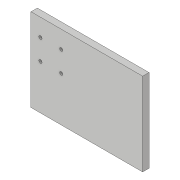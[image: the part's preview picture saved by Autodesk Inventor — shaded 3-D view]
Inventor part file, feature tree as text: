
AUTODESK INVENTOR PART (.ipt)
format: ipt  version: 2019 (Build 230136000, 136)  size: 96,768 bytes
history: native  units: mm
features: sketch x4, extrude x2
ambient origin geometry x8: Origin, YZ Plane, XZ Plane, XY Plane, X Axis, Y Axis, Z Axis, Center Point
bodies: Solid1 (feature_tree)
feature tree (6):
  extrude  "Extrusion1"  Depth=260.0mm
  sketch  "Sketch2"  dims[d2=20.0mm d3=0.0mm d4=30.0mm]
  sketch  "Sketch3"  dims[d5=55.0mm]
  extrude  "Extrusion2"  Depth=20.0mm
  sketch  "Sketch1"  dims[d0=350.0mm d1=260.0mm]
  sketch  "Sketch4"  dims[d6=55.0mm d7=65.0mm d8=65.0mm d9=10.0mm d10=10.0mm d11=10.0mm d12=10.0mm d13=20.0mm d14=0.0mm]
